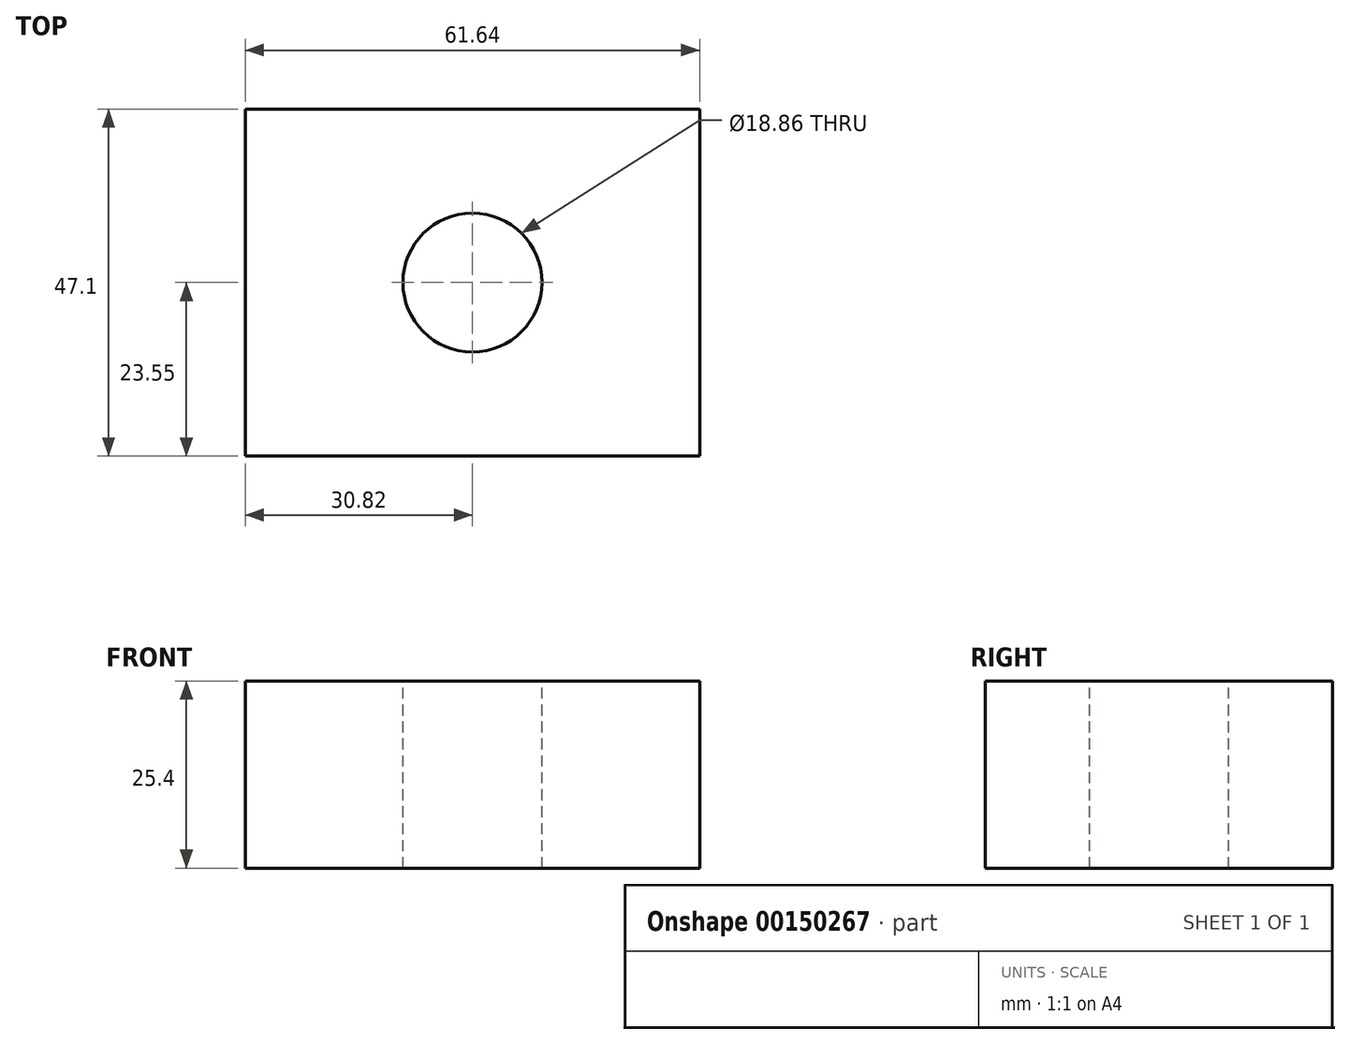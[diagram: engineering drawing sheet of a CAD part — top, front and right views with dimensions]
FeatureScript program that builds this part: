
annotation { "Feature Type Name" : "Feature", "Feature Type Description" : "" }
export const myFeature = defineFeature(function(context is Context, id is Id, definition is map)
    precondition{}
    {
        {
            var Q0;
            Q0=qCreatedBy(makeId("Top.planeOp"),FACE);
            var sketch = newSketch(context, id + "F0", { "sketchPlane" : qUnion([Q0])});
            skLineSegment(sketch, "E0.bottom", {"start": v(30.82, -23.55) * mm, "end": v(-30.82, -23.55) * mm});
            skLineSegment(sketch, "E0.top", {"start": v(30.82, 23.55) * mm, "end": v(-30.82, 23.55) * mm});
            skLineSegment(sketch, "E0.left", {"start": v(30.82, -23.55) * mm, "end": v(30.82, 23.55) * mm});
            skLineSegment(sketch, "E0.right", {"start": v(-30.82, -23.55) * mm, "end": v(-30.82, 23.55) * mm});
            skPoint(sketch, "E0.middle", {"position": v(0, 0) * mm});
            skCircle(sketch, "E1", {"center": v(0, 0) * mm, "radius": 9.43 * mm});
            skSolve(sketch);
        }
        {
            var Q0;
            Q0=makeQuery(id+"F0.imprint","IMPRINT",FACE,{"disambiguationData":[TD([[makeQuery(id+"F0.imprint","IMPRINT",EDGE,{"derivedFrom":sQuery(id+"F0.wireOp",EDGE,"E0.bottom")}),-1.0]])]});
            extrude(context, id + "F1", {"entities" : qUnion([Q0]), "oppositeDirection" : true, "depth" : 25.4 * mm});
        }
    });
